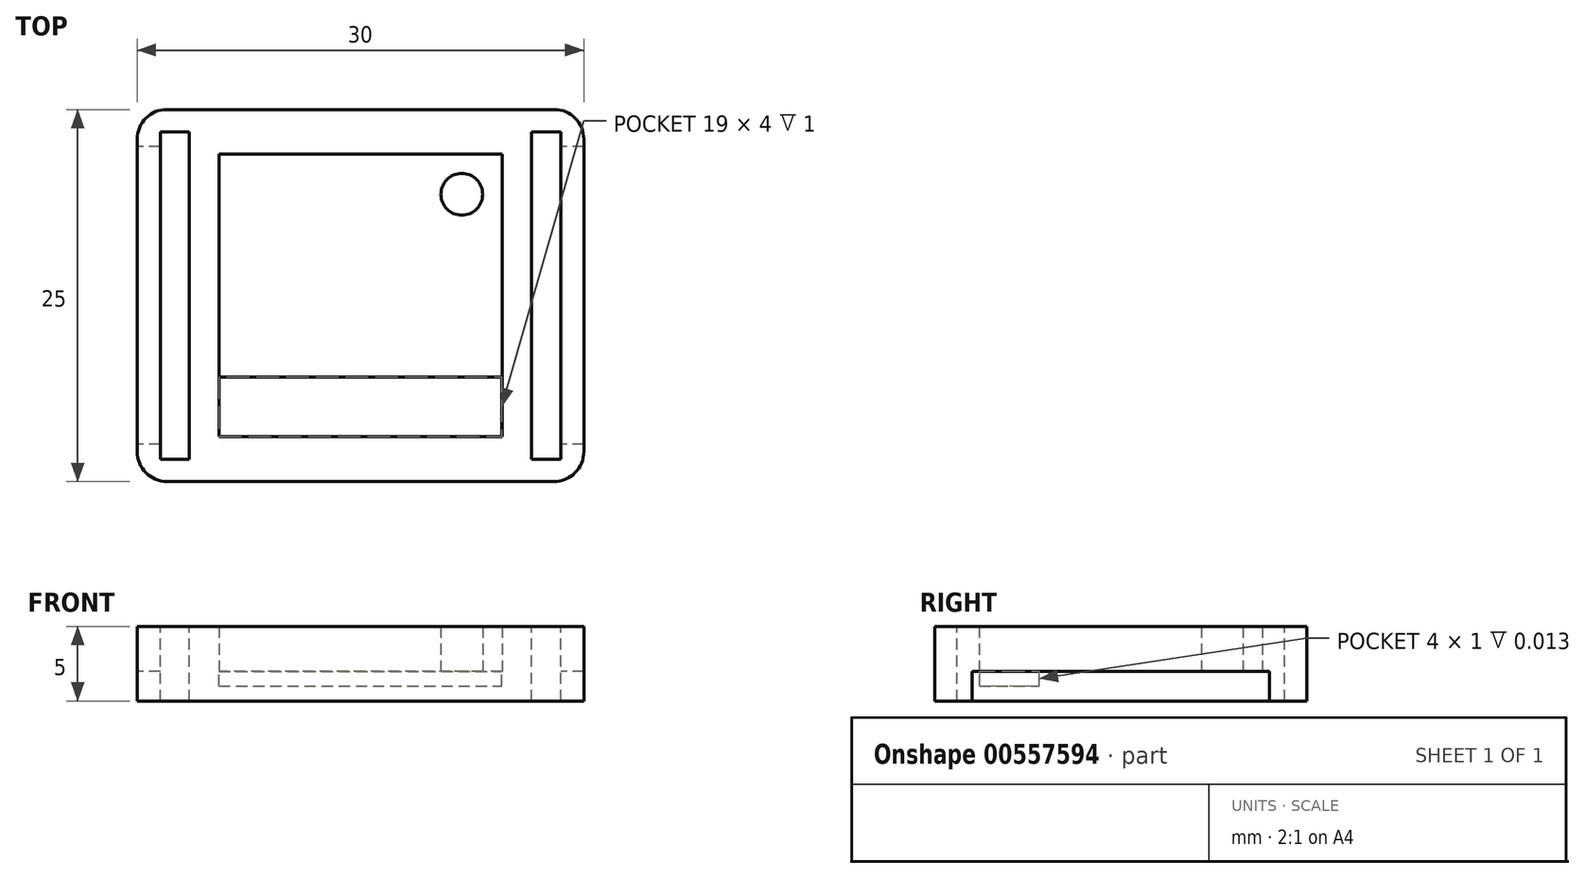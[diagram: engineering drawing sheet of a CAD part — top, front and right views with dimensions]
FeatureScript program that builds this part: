
annotation { "Feature Type Name" : "Feature", "Feature Type Description" : "" }
export const myFeature = defineFeature(function(context is Context, id is Id, definition is map)
    precondition{}
    {
        {
            var Q0;
            Q0=qCreatedBy(makeId("Top.planeOp"),FACE);
            var sketch = newSketch(context, id + "F0", { "sketchPlane" : qUnion([Q0])});
            skLineSegment(sketch, "E0.bottom", {"start": v(15, -12.5) * mm, "end": v(-15, -12.5) * mm});
            skLineSegment(sketch, "E0.top", {"start": v(15, 12.5) * mm, "end": v(-15, 12.5) * mm});
            skLineSegment(sketch, "E0.left", {"start": v(15, -12.5) * mm, "end": v(15, 12.5) * mm});
            skLineSegment(sketch, "E0.right", {"start": v(-15, -12.5) * mm, "end": v(-15, 12.5) * mm});
            skPoint(sketch, "E0.middle", {"position": v(0, 0) * mm});
            skSolve(sketch);
        }
        {
            var Q0;
            Q0 = qSketchRegion(id + "F0", true);
            extrude(context, id + "F1", {"entities" : qUnion([Q0]), "depth" : 3 * mm, "offsetDistance" : 25 * mm});
        }
        {
            var Q0;
            Q0=qCreatedBy(makeId("Top.planeOp"),FACE);
            var sketch = newSketch(context, id + "F2", { "sketchPlane" : qUnion([Q0])});
            skLineSegment(sketch, "E1.bottom", {"start": v(9.5, -9.5) * mm, "end": v(-9.5, -9.5) * mm});
            skLineSegment(sketch, "E1.top", {"start": v(9.5, 9.5) * mm, "end": v(-9.5, 9.5) * mm});
            skLineSegment(sketch, "E1.left", {"start": v(9.5, -9.5) * mm, "end": v(9.5, 9.5) * mm});
            skLineSegment(sketch, "E1.right", {"start": v(-9.5, -9.5) * mm, "end": v(-9.5, 9.5) * mm});
            skPoint(sketch, "E1.middle", {"position": v(0, 0) * mm});
            skSolve(sketch);
        }
        {
            var Q0;
            Q0 = qSketchRegion(id + "F2", true);
            extrude(context, id + "F3", {"entities" : qUnion([Q0]), "operationType" : NewBodyOperationType.REMOVE, "depth" : 5 * mm, "offsetDistance" : 25 * mm});
        }
        {
            var Q0;
            Q0 = qSketchRegion(id + "F0", true);
            extrude(context, id + "F4", {"entities" : qUnion([Q0]), "operationType" : NewBodyOperationType.ADD, "oppositeDirection" : true, "depth" : 2 * mm, "offsetDistance" : 25 * mm});
        }
        {
            var Q0;
            Q0=qCreatedBy(makeId("Top.planeOp"),FACE);
            var sketch = newSketch(context, id + "F5", { "sketchPlane" : qUnion([Q0])});
            skLineSegment(sketch, "E2.bottom", {"start": v(-11.5, -11) * mm, "end": v(-13.45, -11) * mm});
            skLineSegment(sketch, "E2.top", {"start": v(-11.5, 11) * mm, "end": v(-13.45, 11) * mm});
            skLineSegment(sketch, "E2.left", {"start": v(-11.5, -11) * mm, "end": v(-11.5, 11) * mm});
            skLineSegment(sketch, "E2.right", {"start": v(-13.45, -11) * mm, "end": v(-13.45, 11) * mm});
            skPoint(sketch, "E2.middle", {"position": v(-12.47, 0) * mm});
            skLineSegment(sketch, "E3.bottom", {"start": v(13.45, -11) * mm, "end": v(11.5, -11) * mm});
            skLineSegment(sketch, "E3.top", {"start": v(13.45, 11) * mm, "end": v(11.5, 11) * mm});
            skLineSegment(sketch, "E3.left", {"start": v(13.45, -11) * mm, "end": v(13.45, 11) * mm});
            skLineSegment(sketch, "E3.right", {"start": v(11.5, -11) * mm, "end": v(11.5, 11) * mm});
            skPoint(sketch, "E3.middle", {"position": v(12.47, 0) * mm});
            skSolve(sketch);
        }
        {
            var Q0;
            Q0 = qSketchRegion(id + "F5", true);
            extrude(context, id + "F6", {"entities" : qUnion([Q0]), "operationType" : NewBodyOperationType.REMOVE, "endBound" : BoundingType.SYMMETRIC, "oppositeDirection" : true, "depth" : 10 * mm, "offsetDistance" : 25 * mm});
        }
        {
            var Q0;
            {var subQ0=sQuery(id+"F0.wireOp",EDGE,"E0.left");var subQ1=sQuery(id+"F0.wireOp",EDGE,"E0.bottom");Q0=makeQuery(id+"F4.boolean.opBoolean","MERGE",EDGE,{"derivedFrom":[makeQuery(id+"F1.opExtrude","SWEPT_EDGE",EDGE,{"disambiguationData":[OSD([subQ1,subQ0])]}),makeQuery(id+"F4.opExtrude","SWEPT_EDGE",EDGE,{"disambiguationData":[OSD([subQ1,subQ0])]})]});}
            var Q1;
            {var subQ0=sQuery(id+"F0.wireOp",EDGE,"E0.left");var subQ1=sQuery(id+"F0.wireOp",EDGE,"E0.top");Q1=makeQuery(id+"F4.boolean.opBoolean","MERGE",EDGE,{"derivedFrom":[makeQuery(id+"F1.opExtrude","SWEPT_EDGE",EDGE,{"disambiguationData":[OSD([subQ1,subQ0])]}),makeQuery(id+"F4.opExtrude","SWEPT_EDGE",EDGE,{"disambiguationData":[OSD([subQ1,subQ0])]})]});}
            var Q2;
            {var subQ0=sQuery(id+"F0.wireOp",EDGE,"E0.right");var subQ1=sQuery(id+"F0.wireOp",EDGE,"E0.bottom");Q2=makeQuery(id+"F4.boolean.opBoolean","MERGE",EDGE,{"derivedFrom":[makeQuery(id+"F1.opExtrude","SWEPT_EDGE",EDGE,{"disambiguationData":[OSD([subQ1,subQ0])]}),makeQuery(id+"F4.opExtrude","SWEPT_EDGE",EDGE,{"disambiguationData":[OSD([subQ1,subQ0])]})]});}
            var Q3;
            {var subQ0=sQuery(id+"F0.wireOp",EDGE,"E0.right");var subQ1=sQuery(id+"F0.wireOp",EDGE,"E0.top");Q3=makeQuery(id+"F4.boolean.opBoolean","MERGE",EDGE,{"derivedFrom":[makeQuery(id+"F1.opExtrude","SWEPT_EDGE",EDGE,{"disambiguationData":[OSD([subQ1,subQ0])]}),makeQuery(id+"F4.opExtrude","SWEPT_EDGE",EDGE,{"disambiguationData":[OSD([subQ1,subQ0])]})]});}
            fillet(context, id + "F7", {"entities" : qUnion([Q0, Q1, Q2, Q3]), "radius" : 2 * mm, "tangentPropagation" : true, "allowEdgeOverflow" : false});
        }
        {
            var Q0;
            Q0=qCreatedBy(makeId("Top.planeOp"),FACE);
            var sketch = newSketch(context, id + "F8", { "sketchPlane" : qUnion([Q0])});
            skCircle(sketch, "E4", {"center": v(6.8, 6.8) * mm, "radius": 1.4 * mm});
            skSolve(sketch);
        }
        {
            var Q0;
            Q0 = qSketchRegion(id + "F8", true);
            extrude(context, id + "F9", {"entities" : qUnion([Q0]), "operationType" : NewBodyOperationType.ADD, "depth" : 3 * mm, "offsetDistance" : 25 * mm});
        }
        {
            var Q0;
            Q0=qCreatedBy(makeId("Top.planeOp"),FACE);
            var sketch = newSketch(context, id + "F10", { "sketchPlane" : qUnion([Q0])});
            skLineSegment(sketch, "E5.bottom", {"start": v(17.5, -10) * mm, "end": v(12.5, -10) * mm});
            skLineSegment(sketch, "E5.top", {"start": v(17.5, 10) * mm, "end": v(12.5, 10) * mm});
            skLineSegment(sketch, "E5.left", {"start": v(17.5, -10) * mm, "end": v(17.5, 10) * mm});
            skLineSegment(sketch, "E5.right", {"start": v(12.5, -10) * mm, "end": v(12.5, 10) * mm});
            skPoint(sketch, "E5.middle", {"position": v(15, 0) * mm});
            skLineSegment(sketch, "E6.bottom", {"start": v(-12.5, -10) * mm, "end": v(-17.5, -10) * mm});
            skLineSegment(sketch, "E6.top", {"start": v(-12.5, 10) * mm, "end": v(-17.5, 10) * mm});
            skLineSegment(sketch, "E6.left", {"start": v(-12.5, -10) * mm, "end": v(-12.5, 10) * mm});
            skLineSegment(sketch, "E6.right", {"start": v(-17.5, -10) * mm, "end": v(-17.5, 10) * mm});
            skPoint(sketch, "E6.middle", {"position": v(-15, 0) * mm});
            skSolve(sketch);
        }
        {
            var Q0;
            Q0 = qSketchRegion(id + "F10", true);
            extrude(context, id + "F11", {"entities" : qUnion([Q0]), "operationType" : NewBodyOperationType.REMOVE, "oppositeDirection" : true, "depth" : 2 * mm, "offsetDistance" : 25 * mm});
        }
        {
            var Q0;
            Q0=qCreatedBy(makeId("Top.planeOp"),FACE);
            var sketch = newSketch(context, id + "F12", { "sketchPlane" : qUnion([Q0])});
            skLineSegment(sketch, "E7.bottom", {"start": v(-9.51, -9.48) * mm, "end": v(9.49, -9.48) * mm});
            skLineSegment(sketch, "E7.top", {"start": v(-9.51, -5.48) * mm, "end": v(9.49, -5.48) * mm});
            skLineSegment(sketch, "E7.left", {"start": v(-9.51, -9.48) * mm, "end": v(-9.51, -5.48) * mm});
            skLineSegment(sketch, "E7.right", {"start": v(9.49, -9.48) * mm, "end": v(9.49, -5.48) * mm});
            skSolve(sketch);
        }
        {
            var Q0;
            Q0 = qSketchRegion(id + "F12", true);
            extrude(context, id + "F13", {"entities" : qUnion([Q0]), "operationType" : NewBodyOperationType.REMOVE, "oppositeDirection" : true, "depth" : 1 * mm, "offsetDistance" : 25 * mm});
        }
    });
